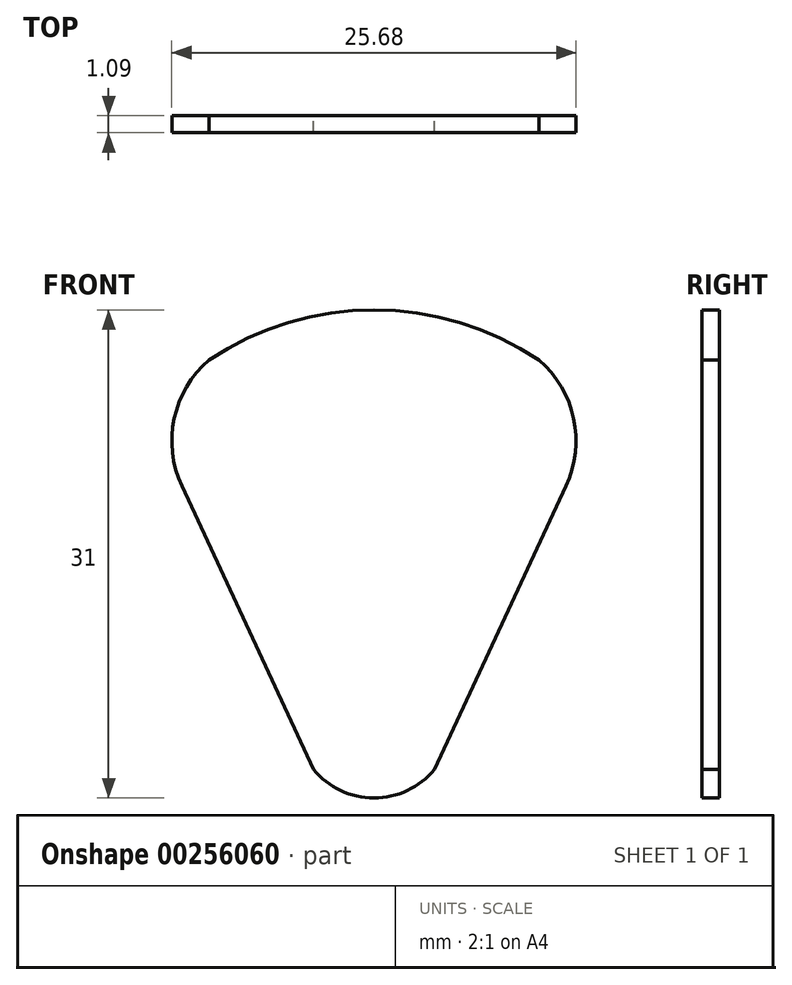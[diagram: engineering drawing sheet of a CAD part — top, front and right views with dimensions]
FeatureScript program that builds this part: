
annotation { "Feature Type Name" : "Feature", "Feature Type Description" : "" }
export const myFeature = defineFeature(function(context is Context, id is Id, definition is map)
    precondition{}
    {
        {
            var Q0;
            Q0=qCreatedBy(makeId("Front.planeOp"),FACE);
            var sketch = newSketch(context, id + "F0", { "sketchPlane" : qUnion([Q0])});
            skLineSegment(sketch, "E0", {"start": v(0, 0) * mm, "end": v(0, 31) * mm});
            skLineSegment(sketch, "E1", {"start": v(3.84, 1.8) * mm, "end": v(12.22, 19.87) * mm});
            skArc(sketch, "E2", {"start": v(0, 0) * mm, "mid": v(2.12, 0.47) * mm, "end": v(3.84, 1.8) * mm});
            skArc(sketch, "E3", {"start": v(10.47, 27.8) * mm, "mid": v(5.48, 30.18) * mm, "end": v(0, 31) * mm});
            skArc(sketch, "E4", {"start": v(12.2, 19.8) * mm, "mid": v(12.69, 24.1) * mm, "end": v(10.47, 27.8) * mm});
            skArc(sketch, "E5.MirrorCS", {"start": v(-10.47, 27.8) * mm, "mid": v(-5.48, 30.18) * mm, "end": v(0, 31) * mm});
            skArc(sketch, "E6.MirrorCS", {"start": v(-12.2, 19.8) * mm, "mid": v(-12.69, 24.1) * mm, "end": v(-10.47, 27.8) * mm});
            skLineSegment(sketch, "E7.MirrorCS", {"start": v(-3.84, 1.8) * mm, "end": v(-12.22, 19.87) * mm});
            skArc(sketch, "E8.MirrorCS", {"start": v(0, 0) * mm, "mid": v(-2.12, 0.47) * mm, "end": v(-3.84, 1.8) * mm});
            skSolve(sketch);
        }
        {
            var Q0;
            Q0 = qSketchRegion(id + "F0", true);
            extrude(context, id + "F1", {"entities" : qUnion([Q0]), "depth" : 1.09 * mm});
        }
    });
